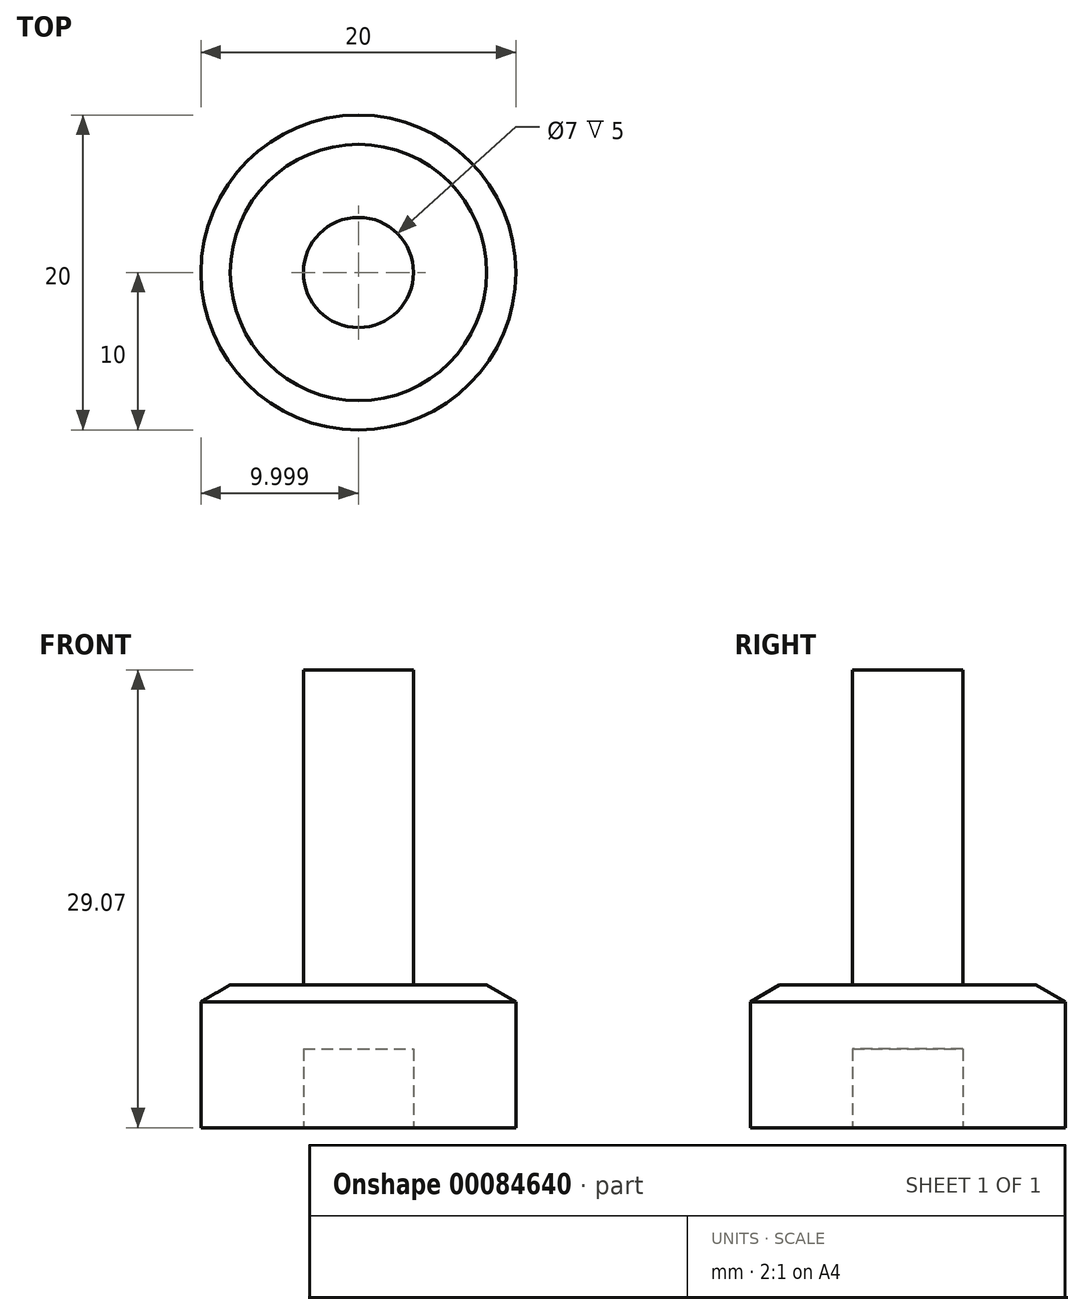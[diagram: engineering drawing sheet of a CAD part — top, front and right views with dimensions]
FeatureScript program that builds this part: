
annotation { "Feature Type Name" : "Feature", "Feature Type Description" : "" }
export const myFeature = defineFeature(function(context is Context, id is Id, definition is map)
    precondition{}
    {
        {
            var Q0;
            Q0=qCreatedBy(makeId("Front.planeOp"),FACE);
            var sketch = newSketch(context, id + "F0", { "sketchPlane" : qUnion([Q0])});
            skLineSegment(sketch, "E0.bottom", {"start": v(-30.55, 8) * mm, "end": v(-20.55, 8) * mm});
            skLineSegment(sketch, "E0.top", {"start": v(-30.55, 0) * mm, "end": v(-24.05, 0) * mm});
            skLineSegment(sketch, "E0.left", {"start": v(-30.55, 8) * mm, "end": v(-30.55, 0) * mm});
            skPoint(sketch, "E1", {"position": v(-20.55, 8) * mm});
            skPoint(sketch, "E2", {"position": v(-20.55, 0) * mm});
            skPoint(sketch, "E3", {"position": v(-20.55, 9.07) * mm});
            skLineSegment(sketch, "E4", {"start": v(-20.55, 8) * mm, "end": v(-20.55, 9.07) * mm});
            skLineSegment(sketch, "E5", {"start": v(-30.55, 8) * mm, "end": v(-28.7, 9.07) * mm});
            skLineSegment(sketch, "E6", {"start": v(-28.7, 9.07) * mm, "end": v(-20.55, 9.07) * mm});
            skLineSegment(sketch, "E7", {"start": v(-20.55, 8) * mm, "end": v(-20.55, 5) * mm});
            skPoint(sketch, "E0.right.end.orphan", {"position": v(-10.55, 0) * mm});
            skPoint(sketch, "E8.start.orphan", {"position": v(-10.55, 8) * mm});
            skLineSegment(sketch, "E9", {"start": v(-20.55, 9.07) * mm, "end": v(-20.55, 29.07) * mm});
            skLineSegment(sketch, "E10", {"start": v(-20.55, 29.07) * mm, "end": v(-24.05, 29.07) * mm});
            skLineSegment(sketch, "E11", {"start": v(-24.05, 29.07) * mm, "end": v(-24.05, 0) * mm});
            skPoint(sketch, "E12.start.orphan", {"position": v(-20.55, 4) * mm});
            skLineSegment(sketch, "E13", {"start": v(-20.55, 5) * mm, "end": v(-24.05, 5) * mm});
            skPoint(sketch, "E14", {"position": v(-20.55, 5) * mm});
            skSolve(sketch);
        }
        {
            var Q0;
            {var subQ0=sQuery(id+"F0.wireOp",EDGE,"E9");Q0=makeQuery(id+"F0.imprint","IMPRINT",FACE,{"disambiguationData":[TD([[makeQuery(id+"F0.imprint","IMPRINT",EDGE,{"derivedFrom":subQ0}),1.0]])]});}
            var Q1;
            {var subQ5=sQuery(id+"F0.wireOp",EDGE,"E0.top");Q1=makeQuery(id+"F0.imprint","IMPRINT",FACE,{"disambiguationData":[TD([[makeQuery(id+"F0.imprint","IMPRINT",EDGE,{"derivedFrom":subQ5}),1.0]])]});}
            var Q2;
            {var subQ0=sQuery(id+"F0.wireOp",EDGE,"E5");Q2=makeQuery(id+"F0.imprint","IMPRINT",FACE,{"disambiguationData":[TD([[makeQuery(id+"F0.imprint","IMPRINT",EDGE,{"derivedFrom":subQ0}),-1.0]])]});}
            var Q3;
            {var subQ0=sQuery(id+"F0.wireOp",EDGE,"E7");Q3=makeQuery(id+"F0.imprint","IMPRINT",FACE,{"disambiguationData":[TD([[makeQuery(id+"F0.imprint","IMPRINT",EDGE,{"derivedFrom":subQ0}),-1.0]])]});}
            var Q4;
            {var subQ0=sQuery(id+"F0.wireOp",EDGE,"E4");Q4=makeQuery(id+"F0.imprint","IMPRINT",FACE,{"disambiguationData":[TD([[makeQuery(id+"F0.imprint","IMPRINT",EDGE,{"derivedFrom":subQ0}),1.0]])]});}
            var Q5;
            Q5=sQuery(id+"F0.wireOp",EDGE,"E9");
            revolve(context, id + "F1", {"entities" : qUnion([Q0, Q1, Q2, Q3, Q4]), "axis" : qUnion([Q5]), "revolveType" : RevolveType.FULL});
        }
    });
